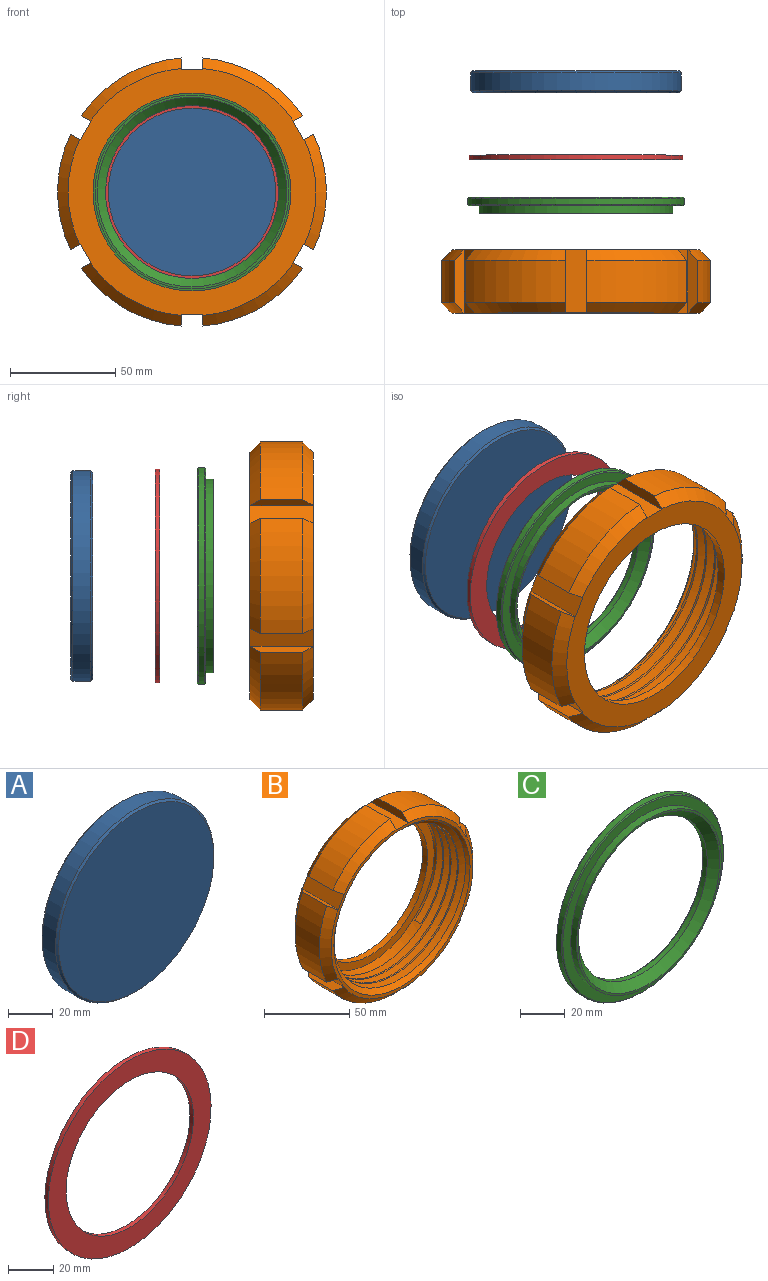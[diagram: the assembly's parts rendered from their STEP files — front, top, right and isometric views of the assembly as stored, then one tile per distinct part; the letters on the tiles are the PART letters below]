
ASSEMBLY  parts=4 mates=3
PART A: 5 faces, bbox 100x10.4x100 mm
  f0: cylinder r=50mm len=100mm, axis (0,1,0), area 2638.9mm2, adj f3,f4
  f1: plane 98x98mm, normal (0,-1,0), area 7543mm2, adj f3
  f2: plane 98x98mm, normal (0,1,0), area 7543mm2, adj f4
  f3: cone r=49mm half-angle=45deg, axis (0,1,0), area 439.8mm2, adj f0,f1
  f4: cone r=50mm half-angle=45deg, axis (0,-1,0), area 439.8mm2, adj f0,f2
PART B: 49 faces, bbox 127.6x32.4x131.3 mm
  f0: cylinder r=63.8mm len=54.94mm, axis (0,1,0), area 1136mm2, adj f7,f13,f40,f43
  f1: cylinder r=63.8mm len=47.58mm, axis (0,1,0), area 1136mm2, adj f8,f14,f39,f42
  f2: cylinder r=63.8mm len=47.58mm, axis (0,1,0), area 1136mm2, adj f9,f15,f33,f41
  f3: cylinder r=63.8mm len=47.58mm, axis (0,1,0), area 1136mm2, adj f10,f16,f37,f38
  f4: cylinder r=63.8mm len=54.94mm, axis (0,1,0), area 1136mm2, adj f11,f17,f34,f36
  f5: cylinder r=63.8mm len=47.58mm, axis (0,1,0), area 1136mm2, adj f12,f18,f32,f35
  f6: plane 117.6x117.17mm, normal (0,-1,0), area 803.5mm2, adj f7,f8,f9,f10,f11,f12,f26,f27
  f7: cone r=58.8mm half-angle=45deg, axis (0,1,0), area 383mm2, adj f0,f6,f40,f43
  f8: cone r=58.8mm half-angle=45deg, axis (0,1,0), area 383mm2, adj f1,f6,f39,f42
  f9: cone r=58.8mm half-angle=45deg, axis (0,1,0), area 383mm2, adj f2,f6,f33,f41
  f10: cone r=58.8mm half-angle=45deg, axis (0,1,0), area 383mm2, adj f3,f6,f37,f38
  f11: cone r=58.8mm half-angle=45deg, axis (0,1,0), area 383mm2, adj f4,f6,f34,f36
  f12: cone r=58.8mm half-angle=45deg, axis (0,1,0), area 383mm2, adj f5,f6,f32,f35
  f13: cone r=63.8mm half-angle=45deg, axis (0,-1,0), area 383mm2, adj f0,f21,f40,f43
  f14: cone r=63.8mm half-angle=45deg, axis (0,-1,0), area 383mm2, adj f1,f21,f39,f42
  f15: cone r=63.8mm half-angle=45deg, axis (0,-1,0), area 383mm2, adj f2,f21,f33,f41
  f16: cone r=63.8mm half-angle=45deg, axis (0,-1,0), area 383mm2, adj f3,f21,f37,f38
  f17: cone r=63.8mm half-angle=45deg, axis (0,-1,0), area 383mm2, adj f4,f21,f34,f36
  f18: cone r=63.8mm half-angle=45deg, axis (0,-1,0), area 383mm2, adj f5,f21,f32,f35
  f19: cylinder r=46.95mm len=93.9mm, axis (0,1,0), area 1239mm2, adj f20,f21
  f20: plane 105x105mm, normal (0,-1,0), area 1734mm2, adj f19,f22
  f21: plane 117.6x117.17mm, normal (0,1,0), area 3907.2mm2, adj f13,f14,f15,f16,f17,f18,f19,f26
  f22: cylinder r=52.5mm len=105mm, axis (0,1,0), area 1551.6mm2, adj f20,f23,f46,f47,f48
  f23: cylinder r=52.5mm len=105mm, axis (0,1,0), area 328.5mm2, adj f22,f24,f47,f48
  f24: cylinder r=52.5mm len=105mm, axis (0,1,0), area 329mm2, adj f23,f25,f47,f48
  f25: cylinder r=52.5mm len=38.38mm, axis (0,1,0), area 27.3mm2, adj f24,f44,f48
  f26: plane 30x8.66mm, normal (-0.87,0,-0.5), area 300mm2, adj f6,f21,f34,f35
  f27: plane 30x8.66mm, normal (-0.87,0,0.5), area 300mm2, adj f6,f21,f36,f37
  f28: plane 30x10mm, normal (0,0,1), area 300mm2, adj f6,f21,f38,f39
  f29: plane 30x8.66mm, normal (0.87,0,0.5), area 300mm2, adj f6,f21,f42,f43
  f30: plane 30x8.66mm, normal (0.87,0,-0.5), area 300mm2, adj f6,f21,f40,f41
  f31: plane 30x10mm, normal (0,0,-1), area 300mm2, adj f6,f21,f32,f33
  f32: plane 30.02x5.38mm, normal (1,0,0), area 136mm2, adj f5,f6,f12,f18,f21,f31
  f33: plane 30.02x5.38mm, normal (-1,0,0), area 136mm2, adj f2,f6,f9,f15,f21,f31
  f34: plane 30.02x4.67mm, normal (0.5,0,-0.87), area 136mm2, adj f4,f6,f11,f17,f21,f26
  f35: plane 30.02x4.67mm, normal (-0.5,0,0.87), area 136mm2, adj f5,f6,f12,f18,f21,f26
  f36: plane 30.02x4.67mm, normal (0.5,0,0.87), area 136mm2, adj f4,f6,f11,f17,f21,f27
  f37: plane 30.02x4.67mm, normal (-0.5,0,-0.87), area 136mm2, adj f3,f6,f10,f16,f21,f27
  f38: plane 30.02x5.38mm, normal (1,0,0), area 136mm2, adj f3,f6,f10,f16,f21,f28
  f39: plane 30.02x5.38mm, normal (-1,0,0), area 136mm2, adj f1,f6,f8,f14,f21,f28
  f40: plane 30.02x4.67mm, normal (-0.5,0,-0.87), area 136mm2, adj f0,f6,f7,f13,f21,f30
  f41: plane 30.02x4.67mm, normal (0.5,0,0.87), area 136mm2, adj f2,f6,f9,f15,f21,f30
  f42: plane 30.02x4.67mm, normal (0.5,0,-0.87), area 136mm2, adj f1,f6,f8,f14,f21,f29
  f43: plane 30.02x4.67mm, normal (-0.5,0,0.87), area 136mm2, adj f0,f6,f7,f13,f21,f29
  f44: cone r=52.5mm half-angle=45deg, axis (0,-1,0), area 1093.8mm2, adj f6,f25,f45,f47,f48
  f45: plane 1.31x0.96mm, normal (0,0,1), area 0.3mm2, adj f44,f47,f48
  f46: plane 5.02x3.24mm, normal (0.74,0,0.67), area 10.8mm2, adj f22,f47,f48
  f47: bspline ~131.25x113.67mm, area 6124.7mm2, adj f22,f23,f24,f44,f45,f46,f48
  f48: bspline ~131.25x113.67mm, area 5430.8mm2, adj f22,f23,f24,f25,f44,f45,f46,f47
PART C: 10 faces, bbox 103x7.7x103 mm
  f0: cylinder r=51.5mm len=103mm, axis (0,1,0), area 970.8mm2, adj f7,f8
  f1: plane 102x102mm, normal (0,-1,0), area 1523.7mm2, adj f3,f7
  f2: plane 102x102mm, normal (0,1,0), area 2629.5mm2, adj f8,f9
  f3: cylinder r=46mm len=92mm, axis (0,1,0), area 1069.4mm2, adj f1,f5
  f4: cylinder r=41mm len=82mm, axis (0,1,0), area 695.5mm2, adj f6,f9
  f5: plane 92x92mm, normal (0,-1,0), area 285.9mm2, adj f3,f6
  f6: cone r=41mm half-angle=45deg, axis (0,-1,0), area 1528.4mm2, adj f4,f5
  f7: cone r=51mm half-angle=45deg, axis (0,1,0), area 227.7mm2, adj f0,f1
  f8: cone r=51.5mm half-angle=45deg, axis (0,-1,0), area 227.7mm2, adj f0,f2
  f9: cone r=42mm half-angle=45deg, axis (0,1,0), area 368.8mm2, adj f2,f4
PART D: 4 faces, bbox 101.5x2.2x101.5 mm
  f0: cylinder r=39.75mm len=79.5mm, axis (0,1,0), area 549.5mm2, adj f2,f3
  f1: cylinder r=50.75mm len=101.5mm, axis (0,1,0), area 701.5mm2, adj f2,f3
  f2: plane 101.5x101.5mm, normal (0,-1,0), area 3127.5mm2, adj f0,f1
  f3: plane 101.5x101.5mm, normal (0,1,0), area 3127.5mm2, adj f0,f1
PLACE A t=(11.99,110.56,-9.46)mm
PLACE B rot(axis=(1,0,0),180deg) t=(11.99,-154.44,-9.46)mm
PLACE C t=(11.99,150.56,-9.46)mm
PLACE D t=(11.99,120.56,-9.46)mm
MATE revolute A.f0 <-> D.f0  axis (0,1,0) through (11.99,110.56,-9.46)mm
MATE revolute C.f0 <-> B.f0  axis (0,1,0) through (11.99,50.56,-9.46)mm
MATE revolute C.f0 <-> D.f0  axis (0,1,0) through (11.99,50.56,-9.46)mm
